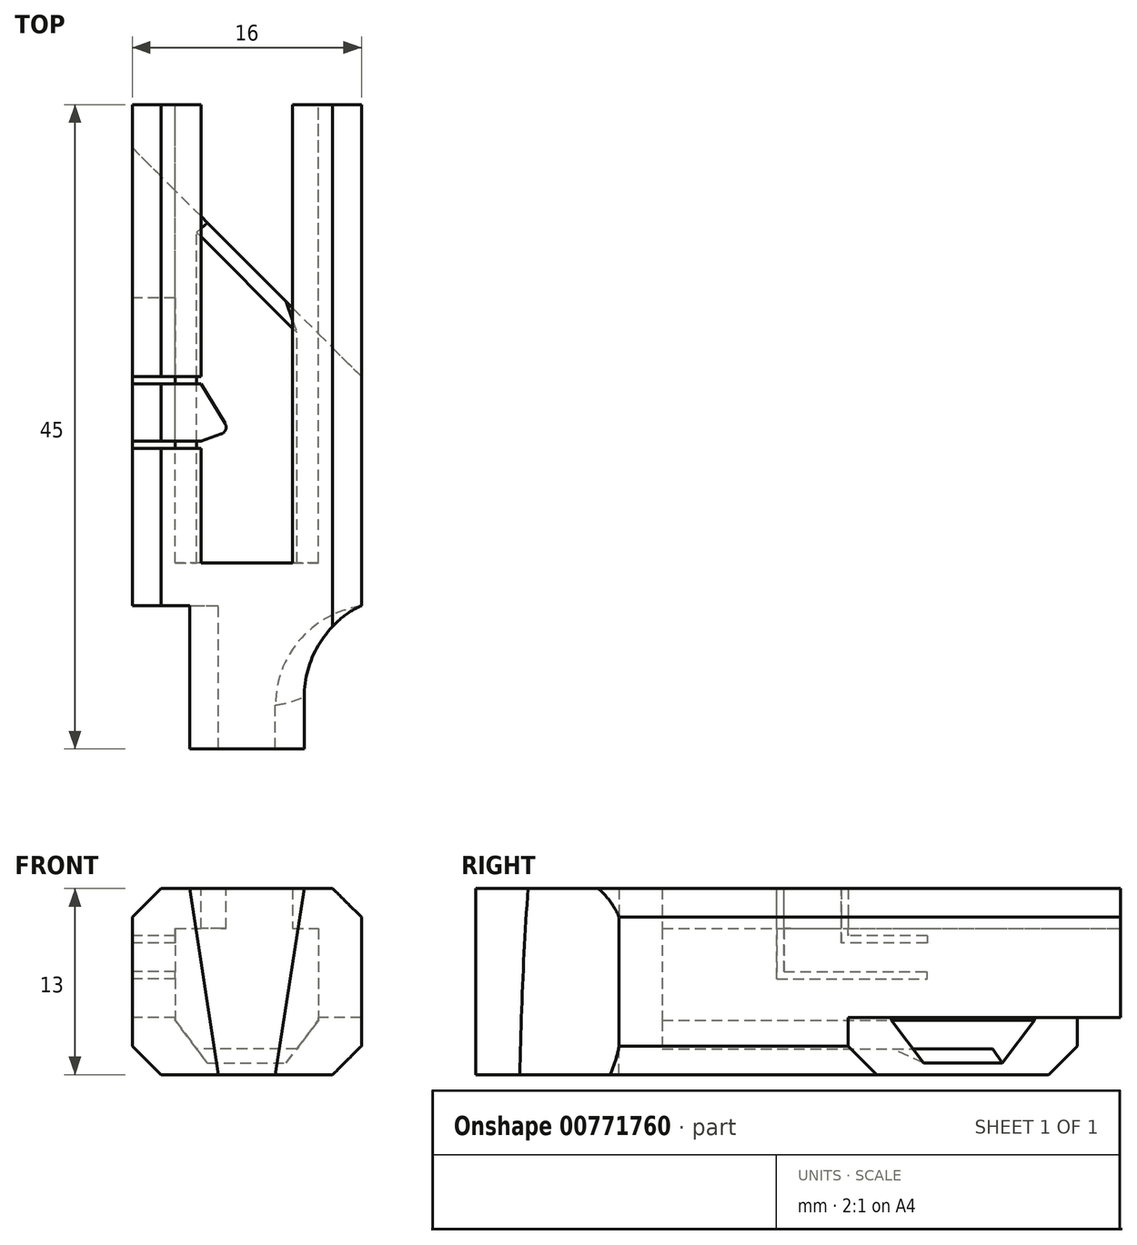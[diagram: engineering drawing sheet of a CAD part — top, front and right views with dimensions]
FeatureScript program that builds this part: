
annotation { "Feature Type Name" : "Feature", "Feature Type Description" : "" }
export const myFeature = defineFeature(function(context is Context, id is Id, definition is map)
    precondition{}
    {
        {
            var Q0;
            Q0=qCreatedBy(makeId("Front.planeOp"),FACE);
            var sketch = newSketch(context, id + "F0", { "sketchPlane" : qUnion([Q0])});
            skLineSegment(sketch, "E0.bottom", {"start": v(-8, 0) * mm, "end": v(8, 0) * mm});
            skLineSegment(sketch, "E0.top", {"start": v(-8, -13) * mm, "end": v(8, -13) * mm});
            skLineSegment(sketch, "E0.left", {"start": v(-8, 0) * mm, "end": v(-8, -13) * mm});
            skLineSegment(sketch, "E0.right", {"start": v(8, 0) * mm, "end": v(8, -13) * mm});
            skSolve(sketch);
        }
        {
            var Q0;
            Q0 = qSketchRegion(id + "F0", true);
            extrude(context, id + "F1", {"entities" : qUnion([Q0]), "depth" : 35 * mm, "offsetDistance" : 25 * mm});
        }
        {
            var Q0;
            Q0=qCreatedBy(makeId("Front.planeOp"),FACE);
            var sketch = newSketch(context, id + "F2", { "sketchPlane" : qUnion([Q0])});
            skLineSegment(sketch, "E1.right", {"start": v(5, -2.8) * mm, "end": v(5, -9.2) * mm});
            skLineSegment(sketch, "E2", {"start": v(3.2, 0) * mm, "end": v(3.2, -2.8) * mm});
            skLineSegment(sketch, "E3", {"start": v(3.2, -2.8) * mm, "end": v(5, -2.8) * mm});
            skLineSegment(sketch, "E4.MirrorCS", {"start": v(-3.2, 0) * mm, "end": v(-3.2, -2.8) * mm});
            skLineSegment(sketch, "E5.MirrorCS", {"start": v(-5, -2.8) * mm, "end": v(-5, -9.2) * mm});
            skLineSegment(sketch, "E6.MirrorCS", {"start": v(-3.2, -2.8) * mm, "end": v(-5, -2.8) * mm});
            skLineSegment(sketch, "E7", {"start": v(-3.2, 0) * mm, "end": v(3.2, 0) * mm});
            skLineSegment(sketch, "E8", {"start": v(0, 0) * mm, "end": v(0, -13.93) * mm, "construction": true});
            skLineSegment(sketch, "E9", {"start": v(5, -9.2) * mm, "end": v(3.5, -11.2) * mm});
            skLineSegment(sketch, "E10.MirrorCS", {"start": v(-5, -9.2) * mm, "end": v(-3.5, -11.2) * mm});
            skLineSegment(sketch, "E11", {"start": v(3.5, -11.2) * mm, "end": v(-3.5, -11.2) * mm});
            skSolve(sketch);
        }
        {
            var Q0;
            Q0 = qSketchRegion(id + "F2", true);
            extrude(context, id + "F3", {"entities" : qUnion([Q0]), "operationType" : NewBodyOperationType.REMOVE, "depth" : 32 * mm, "offsetDistance" : 25 * mm});
        }
        {
            var Q0;
            Q0=qCreatedBy(makeId("Top.planeOp"),FACE);
            var sketch = newSketch(context, id + "F4", { "sketchPlane" : qUnion([Q0])});
            skLineSegment(sketch, "E12", {"start": v(-3.2, -19.5) * mm, "end": v(-1.52, -22.27) * mm});
            skLineSegment(sketch, "E13", {"start": v(-3.2, -23.5) * mm, "end": v(-3.2, -19.5) * mm});
            skLineSegment(sketch, "E14", {"start": v(-3.2, -23.5) * mm, "end": v(-1.78, -23) * mm});
            skPoint(sketch, "E15.visualSharp", {"position": v(-1.2, -22.8) * mm});
            skArc(sketch, "E15.filletArc", {"start": v(-1.78, -23) * mm, "mid": v(-1.48, -22.7) * mm, "end": v(-1.52, -22.27) * mm});
            skSolve(sketch);
        }
        {
            var Q0;
            Q0 = qSketchRegion(id + "F4", true);
            var Q1;
            Q1=makeQuery(id+"F3.boolean.opBoolean","COPY",FACE,{"derivedFrom":makeQuery(id+"F3.opExtrude","SWEPT_FACE",FACE,{"disambiguationData":[OSD([sQuery(id+"F2.wireOp",EDGE,"E3")])]})});
            extrude(context, id + "F5", {"entities" : qUnion([Q0]), "operationType" : NewBodyOperationType.ADD, "endBound" : BoundingType.UP_TO_SURFACE, "oppositeDirection" : true, "depth" : 3 * mm, "endBoundEntityFace" : qUnion([Q1]), "offsetDistance" : 25 * mm});
        }
        {
            var Q0;
            Q0=makeQuery(id+"F1.opExtrude","SWEPT_EDGE",EDGE,{"disambiguationData":[OSD([sQuery(id+"F0.wireOp",EDGE,"E0.bottom"),sQuery(id+"F0.wireOp",EDGE,"E0.right")])]});
            var Q1;
            Q1=makeQuery(id+"F1.opExtrude","SWEPT_EDGE",EDGE,{"disambiguationData":[OSD([sQuery(id+"F0.wireOp",EDGE,"E0.bottom"),sQuery(id+"F0.wireOp",EDGE,"E0.left")])]});
            var Q2;
            Q2=makeQuery(id+"F1.opExtrude","SWEPT_EDGE",EDGE,{"disambiguationData":[OSD([sQuery(id+"F0.wireOp",EDGE,"E0.top"),sQuery(id+"F0.wireOp",EDGE,"E0.left")])]});
            var Q3;
            Q3=makeQuery(id+"F1.opExtrude","SWEPT_EDGE",EDGE,{"disambiguationData":[OSD([sQuery(id+"F0.wireOp",EDGE,"E0.top"),sQuery(id+"F0.wireOp",EDGE,"E0.right")])]});
            chamfer(context, id + "F6", {"entities" : qUnion([Q0, Q1, Q2, Q3]), "width" : 2 * mm, "tangentPropagation" : true});
        }
        {
            var Q0;
            Q0=makeQuery(id+"F1.opExtrude","SWEPT_FACE",FACE,{"disambiguationData":[OSD([sQuery(id+"F0.wireOp",EDGE,"E0.top")])]});
            cPlane(context, id + "F7", {"entities" : qUnion([Q0]), "cplaneType" : CPlaneType.OFFSET, "offset" : 0 * mm, "width" : 150 * mm, "height" : 150 * mm});
        }
        {
            var Q0;
            Q0=qCreatedBy(id+"F7.planeOp",FACE);
            var sketch = newSketch(context, id + "F8", { "sketchPlane" : qUnion([Q0])});
            skLineSegment(sketch, "E16", {"start": v(8, 19) * mm, "end": v(8, 0) * mm});
            skLineSegment(sketch, "E17", {"start": v(8, 0) * mm, "end": v(-8, 0) * mm});
            skLineSegment(sketch, "E18", {"start": v(-8, 0) * mm, "end": v(-8, 3) * mm});
            skLineSegment(sketch, "E19", {"start": v(-8, 3) * mm, "end": v(8, 19) * mm});
            skSolve(sketch);
        }
        {
            var Q0;
            Q0 = qSketchRegion(id + "F8", true);
            extrude(context, id + "F9", {"entities" : qUnion([Q0]), "operationType" : NewBodyOperationType.REMOVE, "oppositeDirection" : true, "depth" : 4 * mm, "offsetDistance" : 25 * mm});
        }
        {
            var Q0;
            Q0=makeQuery(id+"F3.boolean.opBoolean","COPY",EDGE,{"derivedFrom":makeQuery(id+"F3.opExtrude","CAP_EDGE",EDGE,{"disambiguationData":[OSD([sQuery(id+"F2.wireOp",EDGE,"E1.right")])],"isStart":true})});
            var Q1;
            Q1=makeQuery(id+"F3.boolean.opBoolean","COPY",EDGE,{"derivedFrom":makeQuery(id+"F3.opExtrude","CAP_EDGE",EDGE,{"disambiguationData":[OSD([sQuery(id+"F2.wireOp",EDGE,"E5.MirrorCS")])],"isStart":true})});
            var Q2;
            Q2=makeQuery(id+"F3.boolean.opBoolean","COPY",EDGE,{"derivedFrom":makeQuery(id+"F3.opExtrude","CAP_EDGE",EDGE,{"disambiguationData":[OSD([sQuery(id+"F2.wireOp",EDGE,"E6.MirrorCS")])],"isStart":true})});
            var Q3;
            Q3=makeQuery(id+"F3.boolean.opBoolean","COPY",EDGE,{"derivedFrom":makeQuery(id+"F3.opExtrude","CAP_EDGE",EDGE,{"disambiguationData":[OSD([sQuery(id+"F2.wireOp",EDGE,"E3")])],"isStart":true})});
            var Q4;
            Q4=makeQuery(id+"F3.boolean.opBoolean","COPY",EDGE,{"derivedFrom":makeQuery(id+"F3.opExtrude","CAP_EDGE",EDGE,{"disambiguationData":[OSD([sQuery(id+"F2.wireOp",EDGE,"E2")])],"isStart":true})});
            var Q5;
            Q5=makeQuery(id+"F3.boolean.opBoolean","COPY",EDGE,{"derivedFrom":makeQuery(id+"F3.opExtrude","CAP_EDGE",EDGE,{"disambiguationData":[OSD([sQuery(id+"F2.wireOp",EDGE,"E4.MirrorCS")])],"isStart":true})});
            var Q6;
            Q6=makeQuery(id+"F9.boolean.opBoolean","INTERSECT",EDGE,{"derivedFrom":[makeQuery(id+"F3.boolean.opBoolean","COPY",FACE,{"derivedFrom":makeQuery(id+"F3.opExtrude","SWEPT_FACE",FACE,{"disambiguationData":[OSD([sQuery(id+"F2.wireOp",EDGE,"E11")])]})}),makeQuery(id+"F9.opExtrude","SWEPT_FACE",FACE,{"disambiguationData":[OSD([sQuery(id+"F8.wireOp",EDGE,"E19")])]})]});
            chamfer(context, id + "F10", {"entities" : qUnion([Q0, Q1, Q2, Q3, Q4, Q5, Q6]), "width" : 1 * mm, "tangentPropagation" : true});
        }
        {
            var Q0;
            Q0=makeQuery(id+"F1.opExtrude","SWEPT_FACE",FACE,{"disambiguationData":[OSD([sQuery(id+"F0.wireOp",EDGE,"E0.left")])]});
            var sketch = newSketch(context, id + "F11", { "sketchPlane" : qUnion([Q0])});
            skLineSegment(sketch, "E20", {"start": v(19.5, 0) * mm, "end": v(19.5, -3.8) * mm});
            skLineSegment(sketch, "E21", {"start": v(19.5, -3.8) * mm, "end": v(13.5, -3.8) * mm});
            skLineSegment(sketch, "E22", {"start": v(13.5, -5.8) * mm, "end": v(23.5, -5.8) * mm});
            skLineSegment(sketch, "E23", {"start": v(23.5, -5.8) * mm, "end": v(23.5, 0) * mm});
            skLineSegment(sketch, "E24", {"start": v(23.5, 0) * mm, "end": v(19.5, 0) * mm});
            skLineSegment(sketch, "E25.0", {"start": v(13.5, -6.3) * mm, "end": v(24, -6.3) * mm});
            skLineSegment(sketch, "E25.1", {"start": v(24, 0.5) * mm, "end": v(19, 0.5) * mm});
            skLineSegment(sketch, "E25.2", {"start": v(19, 0.5) * mm, "end": v(19, -3.3) * mm});
            skLineSegment(sketch, "E25.3", {"start": v(24, -6.3) * mm, "end": v(24, 0.5) * mm});
            skLineSegment(sketch, "E25.4", {"start": v(19, -3.3) * mm, "end": v(13.5, -3.3) * mm});
            skLineSegment(sketch, "E26", {"start": v(13.5, -3.8) * mm, "end": v(13.5, -3.3) * mm});
            skLineSegment(sketch, "E27", {"start": v(13.5, -5.8) * mm, "end": v(13.5, -6.3) * mm});
            skSolve(sketch);
        }
        {
            var Q0;
            Q0 = qSketchRegion(id + "F11", true);
            var Q1;
            {var subQ0=sQuery(id+"F4.wireOp",EDGE,"E12");Q1=makeQuery(id+"F5.boolean.opBoolean","SPLIT",FACE,{"disambiguationData":[TD([makeQuery(id+"F5.opExtrude","SWEPT_FACE",FACE,{"disambiguationData":[OSD([subQ0])]})])],"derivedFrom":makeQuery(id+"F3.boolean.opBoolean","COPY",FACE,{"derivedFrom":makeQuery(id+"F3.opExtrude","SWEPT_FACE",FACE,{"disambiguationData":[OSD([sQuery(id+"F2.wireOp",EDGE,"E4.MirrorCS")])]})})});}
            extrude(context, id + "F12", {"entities" : qUnion([Q0]), "operationType" : NewBodyOperationType.REMOVE, "endBound" : BoundingType.UP_TO_SURFACE, "oppositeDirection" : true, "depth" : 5 * mm, "endBoundEntityFace" : qUnion([Q1]), "offsetDistance" : 25 * mm});
        }
        {
            var Q0;
            Q0=makeQuery(id+"F1.opExtrude","CAP_FACE",FACE,{"disambiguationData":[OSD([sQuery(id+"F0.wireOp",EDGE,"E0.bottom"),sQuery(id+"F0.wireOp",EDGE,"E0.top"),sQuery(id+"F0.wireOp",EDGE,"E0.left"),sQuery(id+"F0.wireOp",EDGE,"E0.right")])],"isStart":false});
            var sketch = newSketch(context, id + "F13", { "sketchPlane" : qUnion([Q0])});
            skLineSegment(sketch, "E28", {"start": v(-4, 0) * mm, "end": v(-2, -13) * mm});
            skLineSegment(sketch, "E29.MirrorCS", {"start": v(4, 0) * mm, "end": v(2, -13) * mm});
            skLineSegment(sketch, "E30", {"start": v(2, -13) * mm, "end": v(-2, -13) * mm});
            skLineSegment(sketch, "E31", {"start": v(4, 0) * mm, "end": v(-4, 0) * mm});
            skSolve(sketch);
        }
        {
            var Q0;
            Q0=makeQuery(id+"F13.imprint","IMPRINT",FACE,{"disambiguationData":[TD([[makeQuery(id+"F13.imprint","IMPRINT",EDGE,{"derivedFrom":sQuery(id+"F13.wireOp",EDGE,"E28")}),1.0]])]});
            extrude(context, id + "F14", {"entities" : qUnion([Q0]), "operationType" : NewBodyOperationType.ADD, "depth" : 10 * mm, "offsetDistance" : 25 * mm});
        }
        {
            var Q0;
            Q0=makeQuery(id+"F14.opExtrude","CAP_EDGE",EDGE,{"disambiguationData":[OSD([sQuery(id+"F13.wireOp",EDGE,"E28")])],"isStart":true});
            var Q1;
            Q1=makeQuery(id+"F14.opExtrude","CAP_EDGE",EDGE,{"disambiguationData":[OSD([sQuery(id+"F13.wireOp",EDGE,"E29.MirrorCS")])],"isStart":true});
            fillet(context, id + "F15", {"entities" : qUnion([Q0, Q1]), "radius" : 7 * mm, "tangentPropagation" : true, "allowEdgeOverflow" : false});
        }
    });
